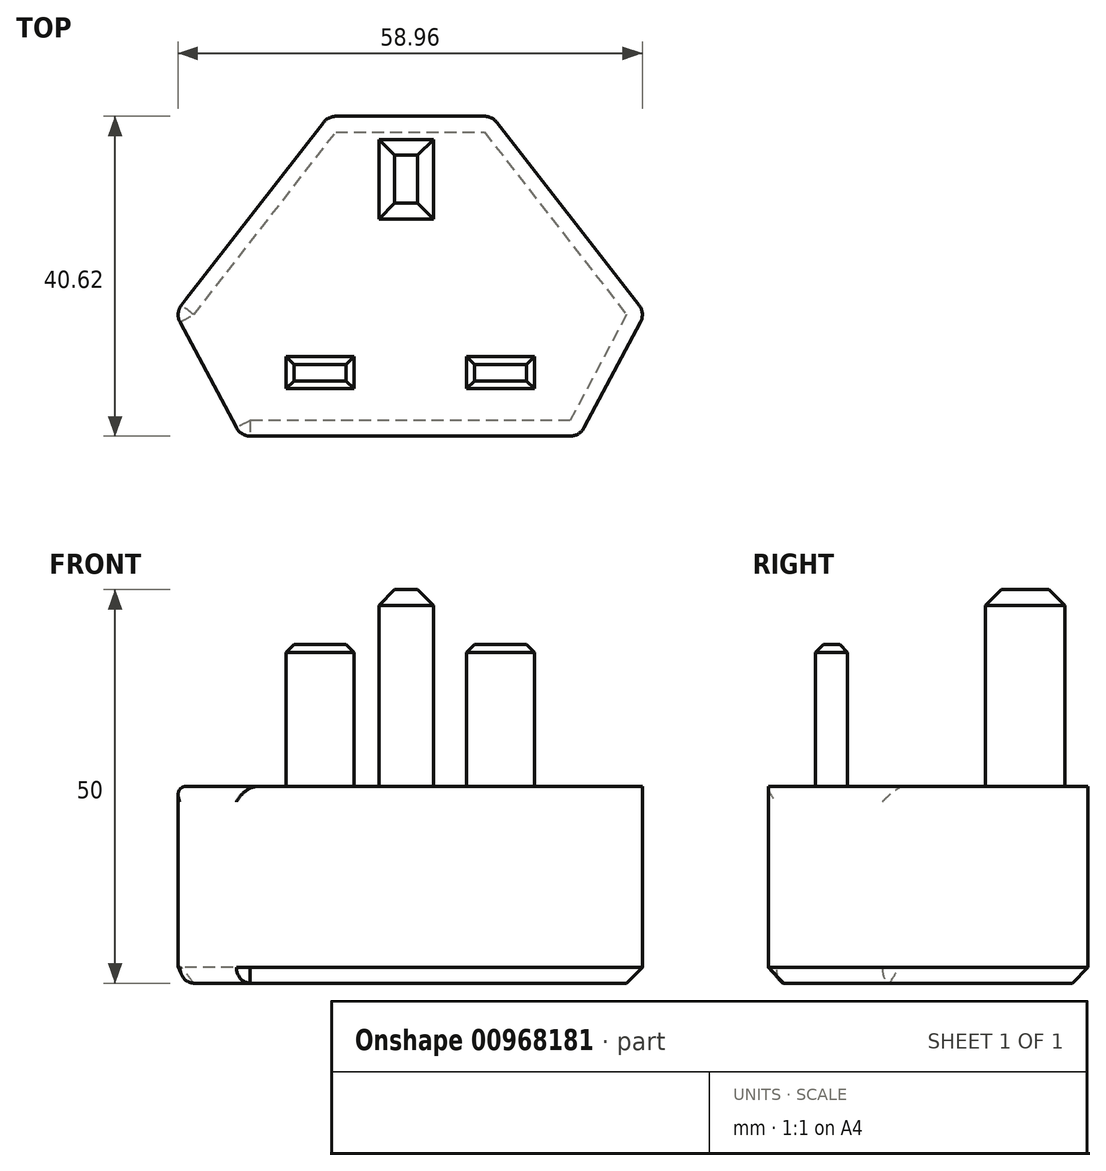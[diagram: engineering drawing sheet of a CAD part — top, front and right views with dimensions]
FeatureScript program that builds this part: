
annotation { "Feature Type Name" : "Feature", "Feature Type Description" : "" }
export const myFeature = defineFeature(function(context is Context, id is Id, definition is map)
    precondition{}
    {
        {
            var Q0;
            Q0=qCreatedBy(makeId("Top.planeOp"),FACE);
            var sketch = newSketch(context, id + "F0", { "sketchPlane" : qUnion([Q0])});
            skLineSegment(sketch, "E0", {"start": v(0, 21.7) * mm, "end": v(10.42, 21.7) * mm});
            skLineSegment(sketch, "E1", {"start": v(10.42, 21.7) * mm, "end": v(29.86, -3.3) * mm});
            skLineSegment(sketch, "E2", {"start": v(29.86, -3.3) * mm, "end": v(21.52, -18.92) * mm});
            skLineSegment(sketch, "E3", {"start": v(21.52, -18.92) * mm, "end": v(0, -18.92) * mm});
            skLineSegment(sketch, "E4", {"start": v(0, 40.44) * mm, "end": v(0, -43.92) * mm, "construction": true});
            skLineSegment(sketch, "E5.MirrorCS", {"start": v(-10.42, 21.7) * mm, "end": v(-29.86, -3.3) * mm});
            skLineSegment(sketch, "E6.MirrorCS", {"start": v(0, 21.7) * mm, "end": v(-10.42, 21.7) * mm});
            skLineSegment(sketch, "E7.MirrorCS", {"start": v(-29.86, -3.3) * mm, "end": v(-21.52, -18.92) * mm});
            skLineSegment(sketch, "E8.MirrorCS", {"start": v(-21.52, -18.92) * mm, "end": v(0, -18.92) * mm});
            skSolve(sketch);
        }
        {
            var Q0;
            Q0=qSketchRegion(id+"F0",true);
            extrude(context, id + "F1", {"entities" : qUnion([Q0]), "depth" : 25 * mm, "offsetDistance" : 25 * mm});
        }
        {
            var Q0;
            Q0=makeQuery(id+"F1.opExtrude","CAP_FACE",FACE,{"disambiguationData":[OSD([sQuery(id+"F0.wireOp",EDGE,"E0"),sQuery(id+"F0.wireOp",EDGE,"E1"),sQuery(id+"F0.wireOp",EDGE,"E2"),sQuery(id+"F0.wireOp",EDGE,"E3"),sQuery(id+"F0.wireOp",EDGE,"E5.MirrorCS"),sQuery(id+"F0.wireOp",EDGE,"E6.MirrorCS"),sQuery(id+"F0.wireOp",EDGE,"E7.MirrorCS"),sQuery(id+"F0.wireOp",EDGE,"E8.MirrorCS")])],"isStart":false});
            var sketch = newSketch(context, id + "F2", { "sketchPlane" : qUnion([Q0])});
            skLineSegment(sketch, "E9.bottom", {"start": v(-4, 8.68) * mm, "end": v(2.95, 8.68) * mm});
            skLineSegment(sketch, "E9.top", {"start": v(-4, 18.75) * mm, "end": v(2.95, 18.75) * mm});
            skLineSegment(sketch, "E9.left", {"start": v(-4, 8.68) * mm, "end": v(-4, 18.75) * mm});
            skLineSegment(sketch, "E9.right", {"start": v(2.95, 8.68) * mm, "end": v(2.95, 18.75) * mm});
            skLineSegment(sketch, "E10", {"start": v(0, -37.15) * mm, "end": v(0, 72.56) * mm, "construction": true});
            skPoint(sketch, "E10.startSnap0", {"position": v(0, -18.92) * mm});
            skSolve(sketch);
        }
        {
            var Q0;
            Q0=makeQuery(id+"F2.imprint","IMPRINT",FACE,{"disambiguationData":[TD([[makeQuery(id+"F2.imprint","IMPRINT",EDGE,{"derivedFrom":sQuery(id+"F2.wireOp",EDGE,"E9.bottom")}),1.0]])]});
            extrude(context, id + "F3", {"entities" : qUnion([Q0]), "operationType" : NewBodyOperationType.ADD, "depth" : 25 * mm, "offsetDistance" : 25 * mm});
        }
        {
            var Q0;
            Q0=makeQuery(id+"F2.imprint","IMPRINT",FACE,{"disambiguationData":[TD([[makeQuery(id+"F2.imprint","IMPRINT",EDGE,{"derivedFrom":sQuery(id+"F2.wireOp",EDGE,"E9.bottom")}),-1.0]])]});
            var sketch = newSketch(context, id + "F4", { "sketchPlane" : qUnion([Q0])});
            skLineSegment(sketch, "E11.bottom", {"start": v(-15.76, -12.9) * mm, "end": v(-7.15, -12.9) * mm});
            skLineSegment(sketch, "E11.top", {"start": v(-15.76, -8.83) * mm, "end": v(-7.15, -8.83) * mm});
            skLineSegment(sketch, "E11.left", {"start": v(-15.76, -12.9) * mm, "end": v(-15.76, -8.83) * mm});
            skLineSegment(sketch, "E11.right", {"start": v(-7.15, -12.9) * mm, "end": v(-7.15, -8.83) * mm});
            skLineSegment(sketch, "E12.MirrorCS", {"start": v(7.15, -12.9) * mm, "end": v(7.15, -8.83) * mm});
            skLineSegment(sketch, "E13.MirrorCS", {"start": v(15.76, -8.83) * mm, "end": v(7.15, -8.83) * mm});
            skLineSegment(sketch, "E14.MirrorCS", {"start": v(15.76, -12.9) * mm, "end": v(15.76, -8.83) * mm});
            skLineSegment(sketch, "E15.MirrorCS", {"start": v(15.76, -12.9) * mm, "end": v(7.15, -12.9) * mm});
            skSolve(sketch);
        }
        {
            var Q0;
            Q0=qSketchRegion(id+"F4",true);
            extrude(context, id + "F5", {"entities" : qUnion([Q0]), "operationType" : NewBodyOperationType.ADD, "depth" : 18 * mm, "offsetDistance" : 25 * mm});
        }
        {
            var Q0;
            Q0=makeQuery(id+"F1.opExtrude","SWEPT_EDGE",EDGE,{"disambiguationData":[OSD([sQuery(id+"F0.wireOp",EDGE,"E2"),sQuery(id+"F0.wireOp",EDGE,"E3")])]});
            var Q1;
            Q1=makeQuery(id+"F1.opExtrude","SWEPT_EDGE",EDGE,{"disambiguationData":[OSD([sQuery(id+"F0.wireOp",EDGE,"E7.MirrorCS"),sQuery(id+"F0.wireOp",EDGE,"E8.MirrorCS")])]});
            var Q2;
            Q2=makeQuery(id+"F1.opExtrude","SWEPT_FACE",FACE,{"disambiguationData":[OSD([sQuery(id+"F0.wireOp",EDGE,"E7.MirrorCS")])]});
            var Q3;
            Q3=makeQuery(id+"F1.opExtrude","SWEPT_EDGE",EDGE,{"disambiguationData":[OSD([sQuery(id+"F0.wireOp",EDGE,"E5.MirrorCS"),sQuery(id+"F0.wireOp",EDGE,"E6.MirrorCS")])]});
            var Q4;
            Q4=makeQuery(id+"F1.opExtrude","SWEPT_EDGE",EDGE,{"disambiguationData":[OSD([sQuery(id+"F0.wireOp",EDGE,"E0"),sQuery(id+"F0.wireOp",EDGE,"E1")])]});
            var Q5;
            Q5=makeQuery(id+"F1.opExtrude","SWEPT_EDGE",EDGE,{"disambiguationData":[OSD([sQuery(id+"F0.wireOp",EDGE,"E1"),sQuery(id+"F0.wireOp",EDGE,"E2")])]});
            fillet(context, id + "F6", {"entities" : qUnion([Q0, Q1, Q2, Q3, Q4, Q5]), "radius" : 2 * mm, "tangentPropagation" : true, "allowEdgeOverflow" : false});
        }
        {
            var Q0;
            Q0=makeQuery(id+"F1.opExtrude","CAP_EDGE",EDGE,{"disambiguationData":[OSD([sQuery(id+"F0.wireOp",EDGE,"E0"),sQuery(id+"F0.wireOp",EDGE,"E6.MirrorCS")])],"isStart":true});
            var Q1;
            Q1=makeQuery(id+"F3.opExtrude","CAP_EDGE",EDGE,{"disambiguationData":[OSD([sQuery(id+"F2.wireOp",EDGE,"E9.left")])],"isStart":false});
            var Q2;
            Q2=makeQuery(id+"F3.opExtrude","CAP_EDGE",EDGE,{"disambiguationData":[OSD([sQuery(id+"F2.wireOp",EDGE,"E9.right")])],"isStart":false});
            var Q3;
            Q3=makeQuery(id+"F3.opExtrude","CAP_EDGE",EDGE,{"disambiguationData":[OSD([sQuery(id+"F2.wireOp",EDGE,"E9.top")])],"isStart":false});
            var Q4;
            Q4=makeQuery(id+"F3.opExtrude","CAP_EDGE",EDGE,{"disambiguationData":[OSD([sQuery(id+"F2.wireOp",EDGE,"E9.bottom")])],"isStart":false});
            chamfer(context, id + "F7", {"entities" : qUnion([Q0, Q1, Q2, Q3, Q4]), "width" : 2 * mm, "tangentPropagation" : true});
        }
        {
            var Q0;
            Q0=makeQuery(id+"F5.opExtrude","CAP_EDGE",EDGE,{"disambiguationData":[OSD([sQuery(id+"F4.wireOp",EDGE,"E15.MirrorCS")])],"isStart":false});
            var Q1;
            Q1=makeQuery(id+"F5.opExtrude","CAP_EDGE",EDGE,{"disambiguationData":[OSD([sQuery(id+"F4.wireOp",EDGE,"E13.MirrorCS")])],"isStart":false});
            var Q2;
            Q2=makeQuery(id+"F5.opExtrude","CAP_EDGE",EDGE,{"disambiguationData":[OSD([sQuery(id+"F4.wireOp",EDGE,"E14.MirrorCS")])],"isStart":false});
            var Q3;
            Q3=makeQuery(id+"F5.opExtrude","CAP_EDGE",EDGE,{"disambiguationData":[OSD([sQuery(id+"F4.wireOp",EDGE,"E12.MirrorCS")])],"isStart":false});
            var Q4;
            Q4=makeQuery(id+"F5.opExtrude","CAP_EDGE",EDGE,{"disambiguationData":[OSD([sQuery(id+"F4.wireOp",EDGE,"E11.bottom")])],"isStart":false});
            var Q5;
            Q5=makeQuery(id+"F5.opExtrude","CAP_EDGE",EDGE,{"disambiguationData":[OSD([sQuery(id+"F4.wireOp",EDGE,"E11.top")])],"isStart":false});
            var Q6;
            Q6=makeQuery(id+"F5.opExtrude","CAP_EDGE",EDGE,{"disambiguationData":[OSD([sQuery(id+"F4.wireOp",EDGE,"E11.left")])],"isStart":false});
            var Q7;
            Q7=makeQuery(id+"F5.opExtrude","CAP_EDGE",EDGE,{"disambiguationData":[OSD([sQuery(id+"F4.wireOp",EDGE,"E11.right")])],"isStart":false});
            chamfer(context, id + "F8", {"entities" : qUnion([Q0, Q1, Q2, Q3, Q4, Q5, Q6, Q7]), "width" : 1 * mm, "tangentPropagation" : true});
        }
    });
